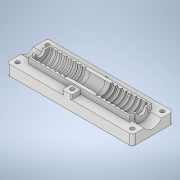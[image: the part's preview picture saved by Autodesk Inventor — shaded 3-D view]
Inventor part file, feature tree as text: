
AUTODESK INVENTOR PART (.ipt)
format: ipt  version: 2020 (Build 240168000, 168)  size: 888,832 bytes
history: native  units: mm
features: sketch x15, extrude x14, projected_geometry x9, other x4, fillet x3, boolean_combine x2, mirror x1
ambient origin geometry x8: Origin, YZ Plane, XZ Plane, XY Plane, X Axis, Y Axis, Z Axis, Center Point
bodies: Volumenkörper1 (feature_tree), Solid2 (feature_tree), Solid3 (feature_tree), Solid4 (feature_tree)
feature tree (48):
  other  "rolinho.ipt"
  extrude  "Extrusion1"  Depth=11.0mm
  other  "Spirale1"
  mirror  "Spiegeln1"
  extrude  "Extrusion5"  Depth=4.0mm
  extrude  "Extrusion6"  Depth=1.0mm
  boolean_combine  "Combine1"
  extrude  "Extrusion7"  Depth=10.0mm TaperAngle=0.0deg
  extrude  "Extrusion8"  Depth=100.0mm TaperAngle=0.0deg
  extrude  "Extrusion9"  Depth=24.0mm
  extrude  "Extrusion10"  Depth=12.0mm TaperAngle=0.0deg
  extrude  "Extrusion11"  Depth=16.0mm
  extrude  "Extrusion12"  Depth=21.0mm
  fillet  "Fillet1"  Radius=4.0mm
  extrude  "Extrusion13"  Depth=3.0mm
  fillet  "Fillet2"  Radius=3.0mm
  extrude  "Extrusion14"  Depth=4.0mm
  extrude  "Extrusion15"  Depth=4.0mm
  extrude  "Extrusion17"  Depth=4.0mm
  fillet  "Fillet3"  Radius=4.0mm
  extrude  "Extrusion18"  Depth=0.5mm
  boolean_combine  "Combine2"
  sketch  "Skizze1"  dims[d0=6.0mm d1=11.0mm]
  sketch  "Skizze3"  dims[d2=36.0mm d3=0.0mm]
  projected_geometry  "Projizierte Kontur2"
  sketch  "Sketch7"  dims[d8=7.0mm d9=24.5mm d10=10.0mm d11=0.0mm d12=90.0deg d13=90.0deg d14=0.0mm d15=0.0mm d16=4.0mm]
  sketch  "Sketch8"  dims[d17=13.962634mm d18=1.0mm]
  sketch  "Sketch9"  dims[d19=0.1mm d32=10.0mm d33=0.0mm]
  projected_geometry  "Projected Loop4"
  sketch  "Sketch10"  dims[d34=7.0mm d35=100.0mm d36=0.0mm]
  projected_geometry  "Projected Loop5"
  projected_geometry  "Projected Loop6"
  projected_geometry  "Projected Loop7"
  projected_geometry  "Projected Loop8"
  sketch  "Sketch11"  dims[d37=82.0mm d38=0.0mm d39=24.0mm]
  projected_geometry  "Projected Loop9"
  sketch  "Sketch12"  dims[d40=30.0mm d41=12.0mm d42=0.0mm]
  sketch  "Sketch13"  dims[d43=74.0mm d44=16.0mm]
  projected_geometry  "Projected Loop10"
  projected_geometry  "Projected Loop11"
  sketch  "Sketch14"  dims[d45=79.0mm d46=21.0mm d47=4.0mm d48=0.0mm]
  sketch  "Sketch15"  dims[d49=3.0mm d50=3.0mm d51=3.0mm]
  sketch  "Sketch16"  dims[d52=3.0mm d53=4.0mm]
  sketch  "Sketch17"  dims[d54=4.0mm d55=4.0mm]
  sketch  "Sketch19"  dims[d56=4.0mm d57=4.0mm d58=4.0mm]
  sketch  "Sketch20"  dims[d59=4.0mm d60=4.0mm d61=10.0mm d62=0.0mm d63=1.0mm d64=1.0mm d65=1.0mm d66=1.0mm d67=6.0mm d68=10.0mm d69=0.0mm d70=10.0mm d71=0.0mm d75=3.0mm d76=3.0mm d77=4.0mm d78=46.0mm d79=4.0mm d80=44.0mm d81=5.5mm d82=5.5mm d83=5.5mm d84=5.5mm d85=5.5mm d86=5.5mm d87=5.0mm d88=0.0mm d89=2.0mm d90=0.5mm d91=6.5mm d92=74.1mm d93=2.1mm d94=0.0mm d95=0.0mm d96=1.0mm d97=12.0mm d98=0.2mm d99=7.9mm d100=0.0mm d101=0.0mm d102=15.0mm d103=0.2mm d104=7.9mm d105=0.0mm d106=0.0mm d110=3.0mm d111=0.0mm d115=1.0mm d116=0.0mm d117=0.0mm d118=7.0mm d119=13.0mm d120=10.0mm d121=0.0mm d122=10.0mm]
  other  "Solid1::rolinho.ipt"
  other  "TaggingFeature1"
